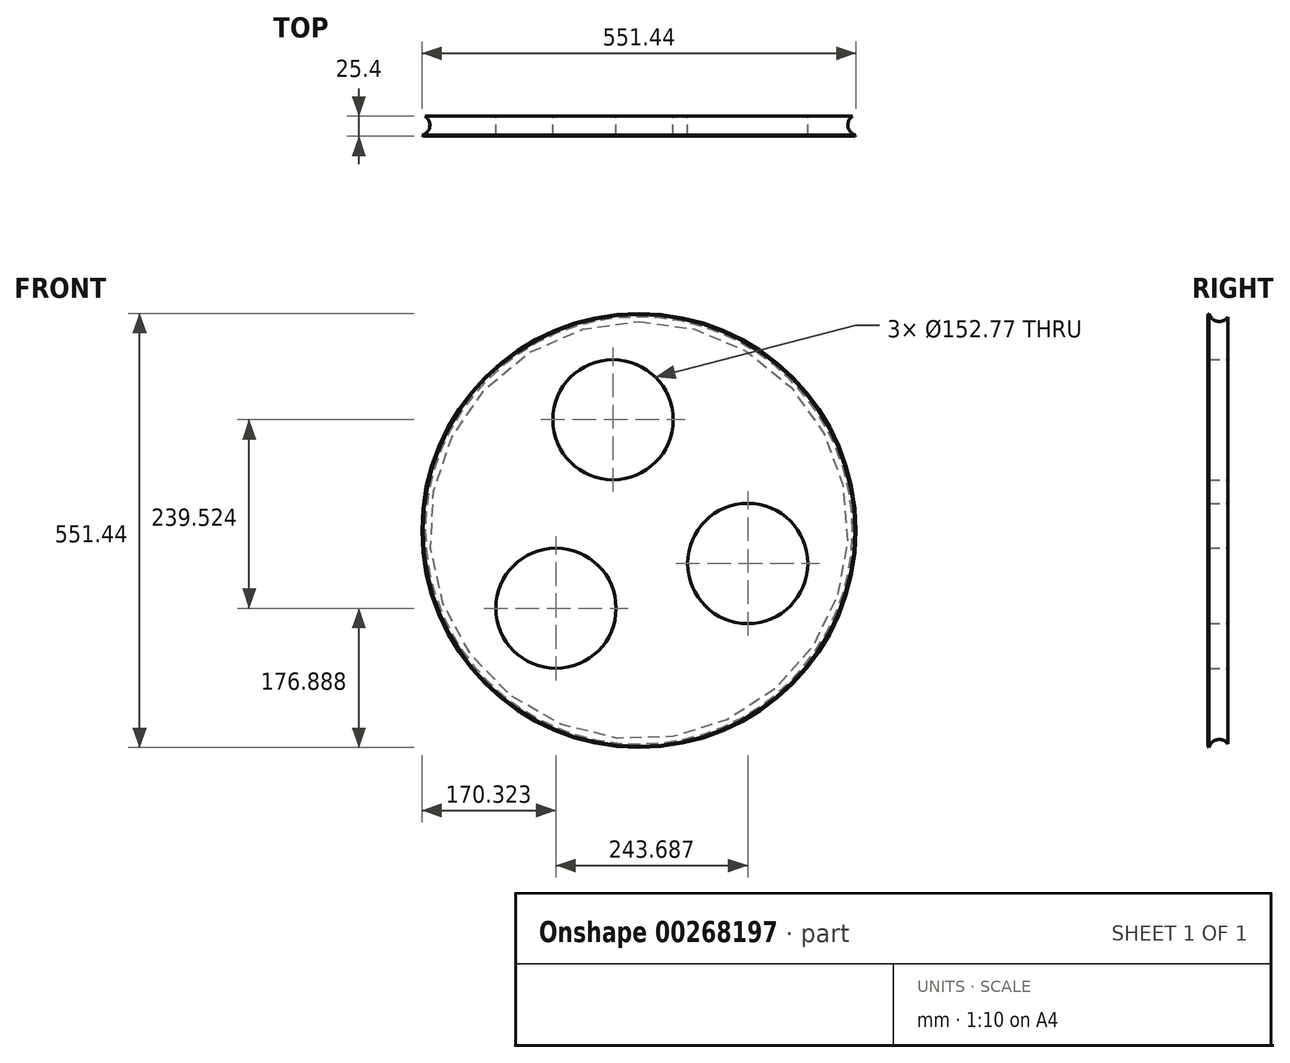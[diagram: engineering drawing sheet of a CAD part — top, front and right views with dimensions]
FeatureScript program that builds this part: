
annotation { "Feature Type Name" : "Feature", "Feature Type Description" : "" }
export const myFeature = defineFeature(function(context is Context, id is Id, definition is map)
    precondition{}
    {
        {
            var Q0;
            Q0=qCreatedBy(makeId("Front.planeOp"),FACE);
            var sketch = newSketch(context, id + "F0", { "sketchPlane" : qUnion([Q0])});
            skCircle(sketch, "E0", {"center": v(0, 0) * mm, "radius": 279.4 * mm});
            skSolve(sketch);
        }
        {
            var Q0;
            Q0 = qSketchRegion(id + "F0", true);
            var Q1;
            Q1=makeQuery(id+"F0.imprint","IMPRINT",FACE,{"disambiguationData":[TD([[makeQuery(id+"F0.imprint","IMPRINT",EDGE,{"derivedFrom":sQuery(id+"F0.wireOp",EDGE,"E0")}),1.0]])]});
            extrude(context, id + "F1", {"entities" : qUnion([Q0, Q1]), "depth" : 25.4 * mm});
        }
        {
            var Q0;
            Q0=qCreatedBy(makeId("Top.planeOp"),FACE);
            var sketch = newSketch(context, id + "F2", { "sketchPlane" : qUnion([Q0])});
            skCircle(sketch, "E1", {"center": v(278.83, -11.03) * mm, "radius": 13.34 * mm});
            skSolve(sketch);
        }
        {
            var Q0;
            Q0=makeQuery(id+"F2.imprint","IMPRINT",FACE,{"disambiguationData":[TD([[makeQuery(id+"F2.imprint","IMPRINT",EDGE,{"derivedFrom":sQuery(id+"F2.wireOp",EDGE,"E1")}),1.0]])]});
            var Q1;
            Q1=makeQuery(id+"F1.opExtrude","SWEPT_FACE",FACE,{"disambiguationData":[OSD([sQuery(id+"F0.wireOp",EDGE,"E0")])]});
            revolve(context, id + "F3", {"operationType" : NewBodyOperationType.REMOVE, "entities" : qUnion([Q0]), "axis" : qUnion([Q1]), "revolveType" : RevolveType.FULL, "oppositeDirection" : true});
        }
        {
            var Q0;
            Q0=makeQuery(id+"F1.opExtrude","CAP_FACE",FACE,{"disambiguationData":[OSD([sQuery(id+"F0.wireOp",EDGE,"E0")])],"isStart":false});
            chamfer(context, id + "F4", {"entities" : qUnion([Q0]), "width" : 5.08 * mm, "tangentPropagation" : true});
        }
        {
            var Q0;
            Q0=makeQuery(id+"F1.opExtrude","CAP_FACE",FACE,{"disambiguationData":[OSD([sQuery(id+"F0.wireOp",EDGE,"E0")])],"isStart":true});
            var sketch = newSketch(context, id + "F5", { "sketchPlane" : qUnion([Q0])});
            skPoint(sketch, "E2", {"position": v(-132.74, -42.66) * mm});
            skPoint(sketch, "E3.1.0", {"position": v(-0.45, -139.42) * mm});
            skPoint(sketch, "E3.2.0", {"position": v(132.46, -43.51) * mm});
            skPoint(sketch, "E3.3.0", {"position": v(82.32, 112.53) * mm});
            skPoint(sketch, "E3.4.0", {"position": v(-81.59, 113.06) * mm});
            skPoint(sketch, "E3.center", {"position": v(0, 0) * mm});
            skSolve(sketch);
        }
        {
            var Q0;
            Q0=makeQuery(id+"F5.imprint","IMPRINT",FACE,{"disambiguationData":[TD([[makeQuery(id+"F5.imprint","IMPRINT",EDGE,{"derivedFrom":makeQuery(id+"F3.boolean.opBoolean","INTERSECT",EDGE,{"derivedFrom":[makeQuery(id+"F1.opExtrude","CAP_FACE",FACE,{"disambiguationData":[OSD([sQuery(id+"F0.wireOp",EDGE,"E0")])],"isStart":true}),makeQuery(id+"F3.opRevolve","SWEPT_FACE",FACE,{"disambiguationData":[OSD([sQuery(id+"F2.wireOp",EDGE,"E1")])]})]})}),-1.0]])]});
            var sketch = newSketch(context, id + "F6", { "sketchPlane" : qUnion([Q0])});
            skCircle(sketch, "E4", {"center": v(-138.29, -41.86) * mm, "radius": 76.38 * mm});
            skCircle(sketch, "E5.1.0", {"center": v(105.4, -98.83) * mm, "radius": 76.38 * mm});
            skCircle(sketch, "E5.2.0", {"center": v(32.9, 140.7) * mm, "radius": 76.38 * mm});
            skPoint(sketch, "E5.center", {"position": v(0, 0) * mm});
            skSolve(sketch);
        }
        {
            var Q0;
            Q0=makeQuery(id+"F6.imprint","IMPRINT",FACE,{"disambiguationData":[TD([[makeQuery(id+"F6.imprint","IMPRINT",EDGE,{"derivedFrom":sQuery(id+"F6.wireOp",EDGE,"E4")}),1.0]])]});
            var Q1;
            Q1=makeQuery(id+"F6.imprint","IMPRINT",FACE,{"disambiguationData":[TD([[makeQuery(id+"F6.imprint","IMPRINT",EDGE,{"derivedFrom":sQuery(id+"F6.wireOp",EDGE,"E5.2.0")}),1.0]])]});
            var Q2;
            Q2=makeQuery(id+"F6.imprint","IMPRINT",FACE,{"disambiguationData":[TD([[makeQuery(id+"F6.imprint","IMPRINT",EDGE,{"derivedFrom":sQuery(id+"F6.wireOp",EDGE,"E5.1.0")}),1.0]])]});
            extrude(context, id + "F7", {"entities" : qUnion([Q0, Q1, Q2]), "operationType" : NewBodyOperationType.REMOVE, "oppositeDirection" : true, "depth" : 25.4 * mm});
        }
    });
